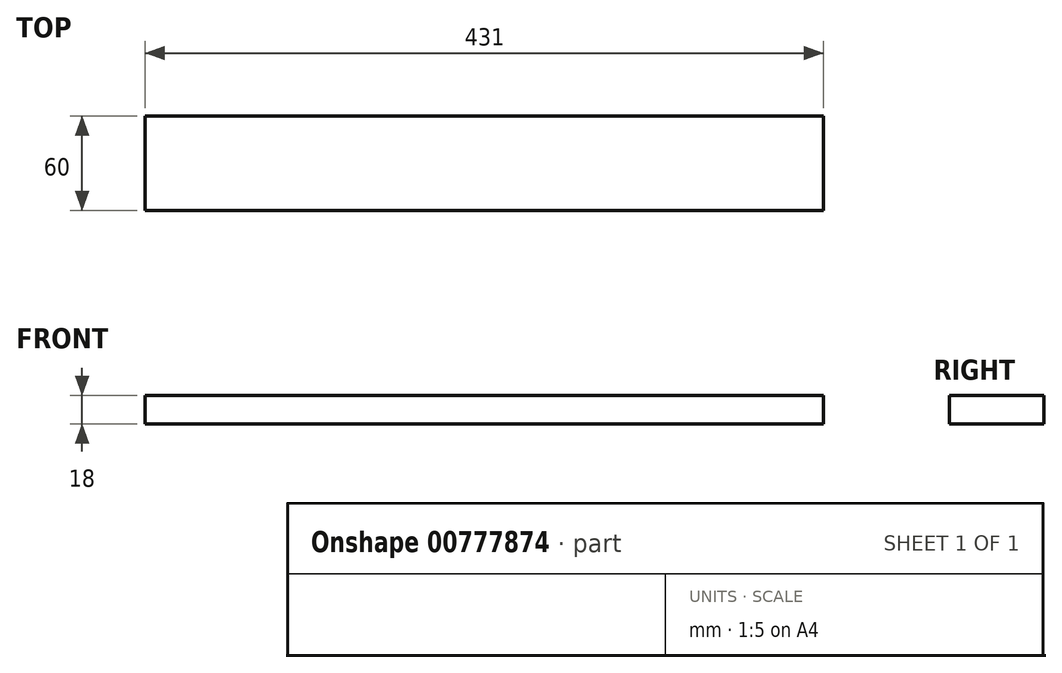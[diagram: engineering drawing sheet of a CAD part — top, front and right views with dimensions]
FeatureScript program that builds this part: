
annotation { "Feature Type Name" : "Feature", "Feature Type Description" : "" }
export const myFeature = defineFeature(function(context is Context, id is Id, definition is map)
    precondition{}
    {
        {
            var Q0;
            Q0=qCreatedBy(makeId("Top.planeOp"),FACE);
            var sketch = newSketch(context, id + "F0", { "sketchPlane" : qUnion([Q0])});
            skLineSegment(sketch, "E0.bottom", {"start": v(-215.5, 30) * mm, "end": v(215.5, 30) * mm});
            skLineSegment(sketch, "E0.top", {"start": v(-215.5, -30) * mm, "end": v(215.5, -30) * mm});
            skLineSegment(sketch, "E0.left", {"start": v(-215.5, 30) * mm, "end": v(-215.5, -30) * mm});
            skLineSegment(sketch, "E0.right", {"start": v(215.5, 30) * mm, "end": v(215.5, -30) * mm});
            skSolve(sketch);
        }
        {
            var Q0;
            Q0 = qSketchRegion(id + "F0", true);
            extrude(context, id + "F1", {"entities" : qUnion([Q0]), "depth" : 18 * mm, "offsetDistance" : 25 * mm});
        }
    });
